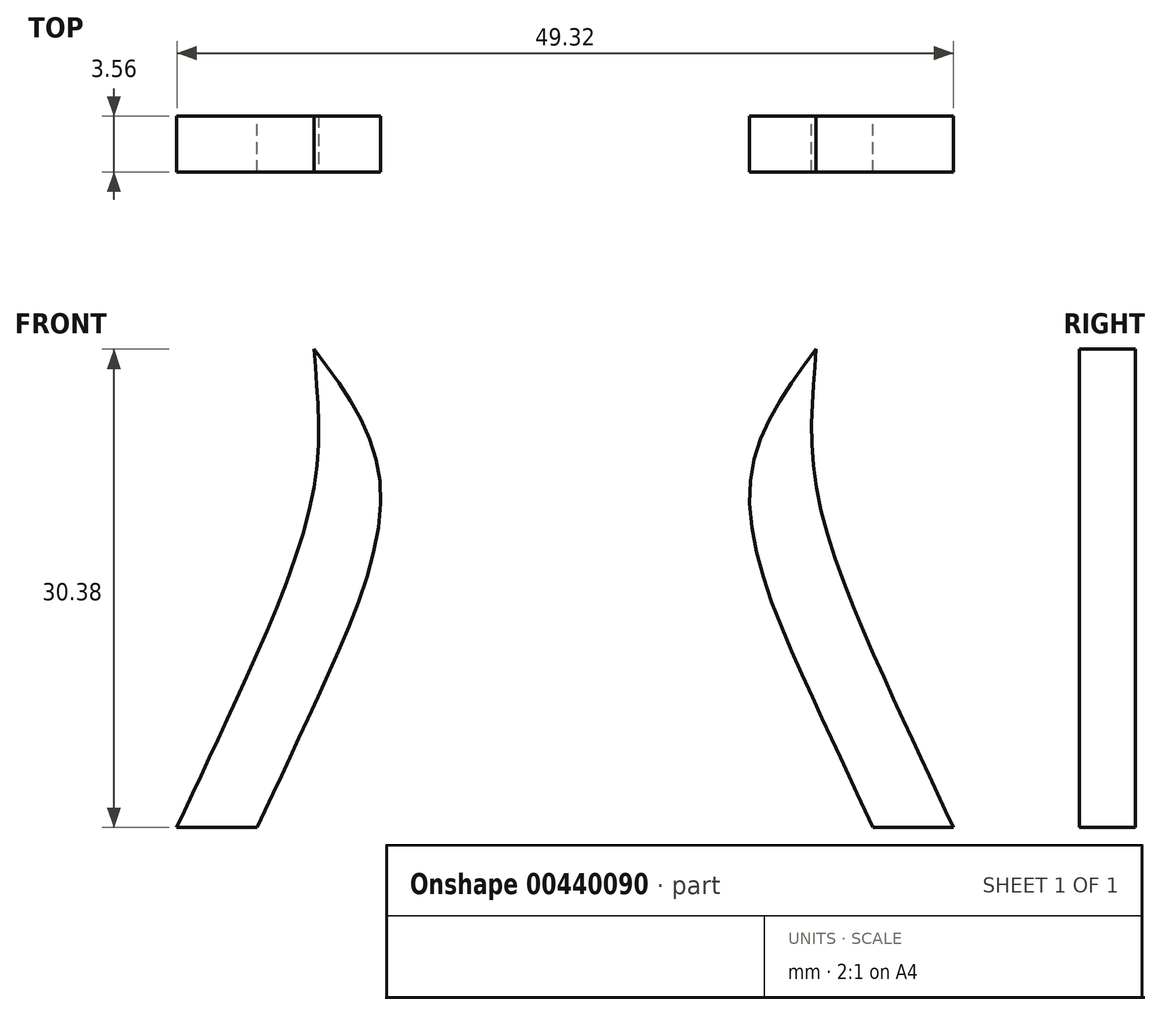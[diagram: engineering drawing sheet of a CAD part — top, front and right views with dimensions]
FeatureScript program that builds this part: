
annotation { "Feature Type Name" : "Feature", "Feature Type Description" : "" }
export const myFeature = defineFeature(function(context is Context, id is Id, definition is map)
    precondition{}
    {
        {
            var Q0;
            Q0=qCreatedBy(makeId("Front.planeOp"),FACE);
            var sketch = newSketch(context, id + "F0", { "sketchPlane" : qUnion([Q0])});
            skFitSpline(sketch, "E0", {"points": [v(-24.66, 0) * mm, v(-20.75, 8.42) * mm, v(-15.94, 21.66) * mm, v(-15.94, 30.38) * mm], "startDerivative": vector(11.6, 24.43) * mm, "endDerivative": vector(-1.64, 25.48) * mm});
            skFitSpline(sketch, "E1", {"points": [v(-19.55, 0) * mm, v(-15.64, 8.42) * mm, v(-11.73, 21.66) * mm, v(-15.94, 30.38) * mm], "startDerivative": vector(11.53, 24.52) * mm, "endDerivative": vector(-18.13, 23.87) * mm});
            skFitSpline(sketch, "E2", {"points": [v(-24.66, 0) * mm, v(-19.55, 0) * mm], "startDerivative": vector(5.11, 0) * mm, "endDerivative": vector(5.11, 0) * mm});
            skFitSpline(sketch, "E3.MirrorCS", {"points": [v(19.55, 0) * mm, v(15.64, 8.42) * mm, v(11.73, 21.66) * mm, v(15.94, 30.38) * mm], "startDerivative": vector(-11.53, 24.52) * mm, "endDerivative": vector(18.13, 23.87) * mm});
            skFitSpline(sketch, "E4.MirrorCS", {"points": [v(24.66, 0) * mm, v(20.75, 8.42) * mm, v(15.94, 21.66) * mm, v(15.94, 30.38) * mm], "startDerivative": vector(-11.6, 24.43) * mm, "endDerivative": vector(1.64, 25.48) * mm});
            skFitSpline(sketch, "E5.MirrorCS", {"points": [v(24.66, 0) * mm, v(19.55, 0) * mm], "startDerivative": vector(-5.11, 0) * mm, "endDerivative": vector(-5.11, 0) * mm});
            skSolve(sketch);
        }
        {
            var Q0;
            Q0=makeQuery(id+"F0.imprint","IMPRINT",FACE,{"disambiguationData":[TD([[makeQuery(id+"F0.imprint","IMPRINT",EDGE,{"derivedFrom":sQuery(id+"F0.wireOp",EDGE,"E0")}),-1.0]])]});
            var Q1;
            Q1=makeQuery(id+"F0.imprint","IMPRINT",FACE,{"disambiguationData":[TD([[makeQuery(id+"F0.imprint","IMPRINT",EDGE,{"derivedFrom":sQuery(id+"F0.wireOp",EDGE,"E3.MirrorCS")}),-1.0]])]});
            extrude(context, id + "F1", {"entities" : qUnion([Q0, Q1]), "depth" : 3.56 * mm});
        }
    });
